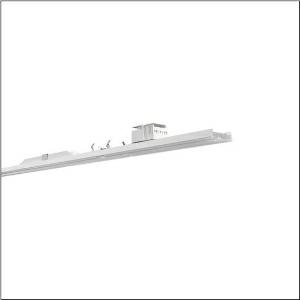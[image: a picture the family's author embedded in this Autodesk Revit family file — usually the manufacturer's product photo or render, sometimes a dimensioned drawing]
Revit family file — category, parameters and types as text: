
# Revit family: licross_r__11_recessed_ho_51tl12dv4m1l_5f58
name_source: partatom
category: Lighting Fixtures
units: mm (PartAtom-declared; Revit-internal decimal feet)

## family parameters
Cut with Voids When Loaded = No
Host = Face
Light Source = No
Part Type = Normal
Room Calculation Point = No
Round Connector Dimension = Use Diameter
Shared = No

## types (1)
- --- (1 x LED, 26230 lm, 150.2 W, 4000K)
    Apparent Load = 150 VA
    CIE Flux Codes = 66 91 98 100 100
    Color Rendering = 80
    Color Temperature = 4000K
    Default Elevation = 1800 mm
    Description = Licross® 11 Recessed HOluminaire insert, length: 2.250mm, width: 66mm, height: 67mm, LED rated luminous flux: 26.230lm, light colour: 840, control gear: DALI 2, control gear: ECG DALI, with plug, 5-pole, with phase selection, mains connection: 220..240V, AC, 50/60Hz, halogen-free wiring, primary optical cover: cover, of PMMA, light emission: direct distribution, protection rating (complete): IP40, insulation class (complete): insulation class I (protective earthing), certification: CE, ENEC, VDE, protection symbol: D if used in an environment without relevant dust loads with corresponding accessories, permissible ambient temperature for indoor applications: -35..+35°C, corresponds to IFS (International Featured Standards) requirements for safety and quality in the food industry, reducing of maximum allowable ambient temperature of 5°C with ceiling mounting, packaging unit: 1 piece
    Height = 58 mm
    Lamp = 1 x LED
    Lamp Light Flux = 26230 lm
    Lamp Power = 150.2 W
    Lamp count = 1
    Length = 2250 mm
    Luminous efficacy = 175 lm/W
    Manufacturer = Siteco
    ModVariant = No
    Model = 51TL12DV4M1L
    Mounting Place = Ceiling
    Mounting Type = Pendant
    Number of Poles = 1
    OnlyDefault = Yes
    Power Factor = 1
    Product Name = Licross® 11 Recessed HO
    Product group = luminaire insert
    ProductGroupID = 902
    Protection Class = Protection class I
    Protection Degree = IP 40
    RLX_Detail_Level = 1
    RlxData = <blob elided: 27621 chars, md5=3bf57332>
    Socket = socket
    Standby Power = 0 W
    System Light Flux = 26229 lm
    System Power = 150 W
    Type Comments = factory setting: luminous flux: 100 % | dim-lin: 254 | 575 mA
    Type Image = l_1266722.jpg
    URL = http://relux.com
    VarID = @adj_133204
    Voltage = 0 V
    Weight = 0.00 kg
    Width = 66 mm

## geometry (parser evidence)
native form markers: Blend x4, Sweep x10
no freeform markers — native parametric forms only
